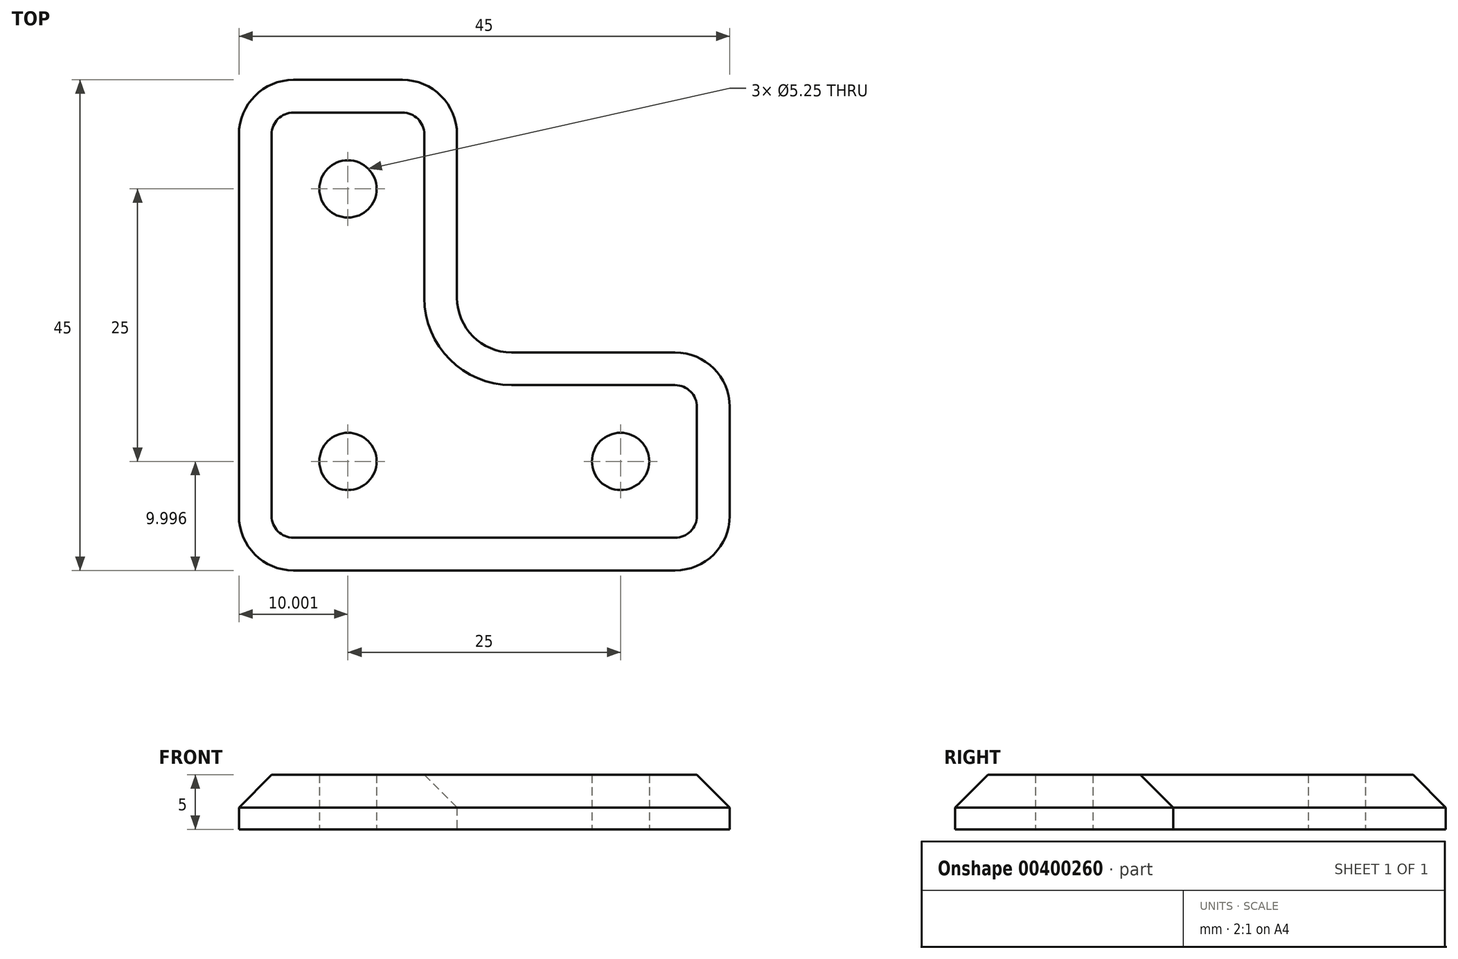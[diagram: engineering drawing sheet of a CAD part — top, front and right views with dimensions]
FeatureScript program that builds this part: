
annotation { "Feature Type Name" : "Feature", "Feature Type Description" : "" }
export const myFeature = defineFeature(function(context is Context, id is Id, definition is map)
    precondition{}
    {
        {
            var Q0;
            Q0=qCreatedBy(makeId("Top.planeOp"),FACE);
            var sketch = newSketch(context, id + "F0", { "sketchPlane" : qUnion([Q0])});
            skLineSegment(sketch, "E0.bottom", {"start": v(9.93, 6.7) * mm, "end": v(44.93, 6.7) * mm});
            skLineSegment(sketch, "E0.top", {"start": v(29.93, 26.7) * mm, "end": v(44.93, 26.7) * mm});
            skLineSegment(sketch, "E0.left", {"start": v(4.93, 11.7) * mm, "end": v(4.93, 26.7) * mm});
            skLineSegment(sketch, "E0.right", {"start": v(49.93, 11.7) * mm, "end": v(49.93, 21.7) * mm});
            skLineSegment(sketch, "E1.top", {"start": v(9.93, 51.7) * mm, "end": v(19.93, 51.7) * mm});
            skLineSegment(sketch, "E1.left", {"start": v(4.93, 26.7) * mm, "end": v(4.93, 46.7) * mm});
            skLineSegment(sketch, "E1.right", {"start": v(24.93, 31.7) * mm, "end": v(24.93, 46.7) * mm});
            skPoint(sketch, "E2.orphan", {"position": v(4.93, 16.7) * mm});
            skCircle(sketch, "E3", {"center": v(14.93, 41.7) * mm, "radius": 2.62 * mm});
            skCircle(sketch, "E4", {"center": v(39.93, 16.7) * mm, "radius": 2.62 * mm});
            skCircle(sketch, "E5", {"center": v(14.93, 16.7) * mm, "radius": 2.62 * mm});
            skPoint(sketch, "E6.orphan", {"position": v(14.93, 51.7) * mm});
            skPoint(sketch, "E7.orphan", {"position": v(49.93, 16.7) * mm});
            skPoint(sketch, "E8.visualSharp", {"position": v(4.93, 6.7) * mm});
            skArc(sketch, "E8.filletArc", {"start": v(4.93, 11.7) * mm, "mid": v(6.4, 8.17) * mm, "end": v(9.93, 6.7) * mm});
            skPoint(sketch, "E9.visualSharp", {"position": v(49.93, 6.7) * mm});
            skArc(sketch, "E9.filletArc", {"start": v(44.93, 6.7) * mm, "mid": v(48.47, 8.17) * mm, "end": v(49.93, 11.7) * mm});
            skPoint(sketch, "E10.visualSharp", {"position": v(49.93, 26.7) * mm});
            skArc(sketch, "E10.filletArc", {"start": v(49.93, 21.7) * mm, "mid": v(48.47, 25.24) * mm, "end": v(44.93, 26.7) * mm});
            skPoint(sketch, "E11.visualSharp", {"position": v(24.93, 51.7) * mm});
            skArc(sketch, "E11.filletArc", {"start": v(24.93, 46.7) * mm, "mid": v(23.47, 50.24) * mm, "end": v(19.93, 51.7) * mm});
            skPoint(sketch, "E12.visualSharp", {"position": v(4.93, 51.7) * mm});
            skArc(sketch, "E12.filletArc", {"start": v(9.93, 51.7) * mm, "mid": v(6.4, 50.24) * mm, "end": v(4.93, 46.7) * mm});
            skPoint(sketch, "E13.visualSharp", {"position": v(24.93, 26.7) * mm});
            skArc(sketch, "E13.filletArc", {"start": v(24.93, 31.7) * mm, "mid": v(26.4, 28.17) * mm, "end": v(29.93, 26.7) * mm});
            skLineSegment(sketch, "E14", {"start": v(14.93, 51.7) * mm, "end": v(14.93, 6.7) * mm, "construction": true});
            skLineSegment(sketch, "E15", {"start": v(4.93, 16.7) * mm, "end": v(49.93, 16.7) * mm, "construction": true});
            skSolve(sketch);
        }
        {
            var Q0;
            Q0 = qSketchRegion(id + "F0", true);
            extrude(context, id + "F1", {"entities" : qUnion([Q0]), "depth" : 5 * mm});
        }
        {
            var Q0;
            Q0=makeQuery(id+"F1.opExtrude","CAP_EDGE",EDGE,{"disambiguationData":[OSD([sQuery(id+"F0.wireOp",EDGE,"E1.top")])],"isStart":false});
            var Q1;
            Q1=makeQuery(id+"F1.opExtrude","CAP_EDGE",EDGE,{"disambiguationData":[OSD([sQuery(id+"F0.wireOp",EDGE,"E11.filletArc")])],"isStart":false});
            var Q2;
            Q2=makeQuery(id+"F1.opExtrude","CAP_EDGE",EDGE,{"disambiguationData":[OSD([sQuery(id+"F0.wireOp",EDGE,"E1.right")])],"isStart":false});
            var Q3;
            Q3=makeQuery(id+"F1.opExtrude","CAP_EDGE",EDGE,{"disambiguationData":[OSD([sQuery(id+"F0.wireOp",EDGE,"E13.filletArc")])],"isStart":false});
            var Q4;
            Q4=makeQuery(id+"F1.opExtrude","CAP_EDGE",EDGE,{"disambiguationData":[OSD([sQuery(id+"F0.wireOp",EDGE,"E0.top")])],"isStart":false});
            var Q5;
            Q5=makeQuery(id+"F1.opExtrude","CAP_EDGE",EDGE,{"disambiguationData":[OSD([sQuery(id+"F0.wireOp",EDGE,"E10.filletArc")])],"isStart":false});
            var Q6;
            Q6=makeQuery(id+"F1.opExtrude","CAP_EDGE",EDGE,{"disambiguationData":[OSD([sQuery(id+"F0.wireOp",EDGE,"E0.right")])],"isStart":false});
            var Q7;
            Q7=makeQuery(id+"F1.opExtrude","CAP_EDGE",EDGE,{"disambiguationData":[OSD([sQuery(id+"F0.wireOp",EDGE,"E9.filletArc")])],"isStart":false});
            var Q8;
            Q8=makeQuery(id+"F1.opExtrude","CAP_EDGE",EDGE,{"disambiguationData":[OSD([sQuery(id+"F0.wireOp",EDGE,"E0.bottom")])],"isStart":false});
            var Q9;
            Q9=makeQuery(id+"F1.opExtrude","CAP_EDGE",EDGE,{"disambiguationData":[OSD([sQuery(id+"F0.wireOp",EDGE,"E8.filletArc")])],"isStart":false});
            var Q10;
            Q10=makeQuery(id+"F1.opExtrude","CAP_EDGE",EDGE,{"disambiguationData":[OSD([sQuery(id+"F0.wireOp",EDGE,"E0.left"),sQuery(id+"F0.wireOp",EDGE,"E1.left")])],"isStart":false});
            var Q11;
            Q11=makeQuery(id+"F1.opExtrude","CAP_EDGE",EDGE,{"disambiguationData":[OSD([sQuery(id+"F0.wireOp",EDGE,"E12.filletArc")])],"isStart":false});
            chamfer(context, id + "F2", {"entities" : qUnion([Q0, Q1, Q2, Q3, Q4, Q5, Q6, Q7, Q8, Q9, Q10, Q11]), "width" : 3 * mm, "tangentPropagation" : true});
        }
    });
